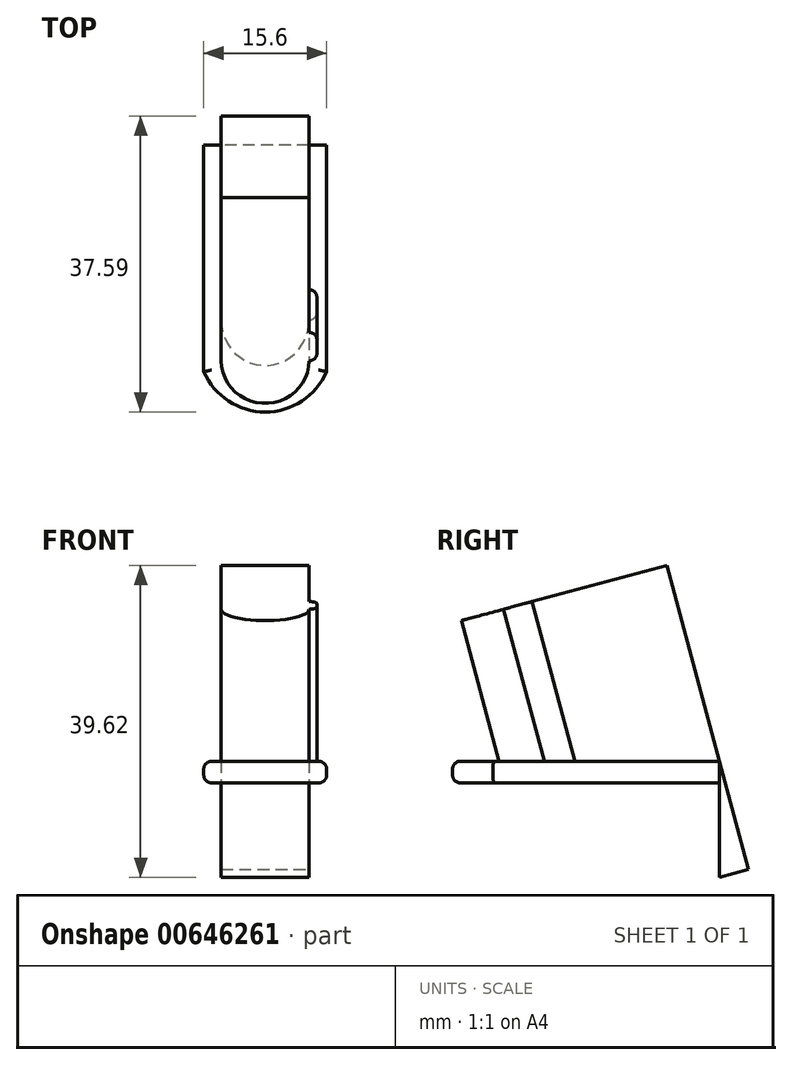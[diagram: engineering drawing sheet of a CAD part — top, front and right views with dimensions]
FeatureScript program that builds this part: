
annotation { "Feature Type Name" : "Feature", "Feature Type Description" : "" }
export const myFeature = defineFeature(function(context is Context, id is Id, definition is map)
    precondition{}
    {
        {
            var Q0;
            Q0=qCreatedBy(makeId("Top.planeOp"),FACE);
            var sketch = newSketch(context, id + "F0", { "sketchPlane" : qUnion([Q0])});
            skLineSegment(sketch, "E0.bottom", {"start": v(-7.8, 16.95) * mm, "end": v(7.8, 16.95) * mm});
            skLineSegment(sketch, "E0.top", {"start": v(-7.8, -16.95) * mm, "end": v(7.8, -16.95) * mm});
            skLineSegment(sketch, "E0.left", {"start": v(-7.8, 16.95) * mm, "end": v(-7.8, -16.95) * mm});
            skLineSegment(sketch, "E0.right", {"start": v(7.8, 16.95) * mm, "end": v(7.8, -16.95) * mm});
            skLineSegment(sketch, "E1.bottom", {"start": v(-5.58, 16.95) * mm, "end": v(5.58, 16.95) * mm});
            skLineSegment(sketch, "E1.top", {"start": v(-5.57, -5.28) * mm, "end": v(5.58, -5.28) * mm});
            skLineSegment(sketch, "E1.left", {"start": v(-5.58, 16.95) * mm, "end": v(-5.57, -5.28) * mm});
            skLineSegment(sketch, "E1.right", {"start": v(5.57, 16.95) * mm, "end": v(5.58, -5.28) * mm});
            skArc(sketch, "E2", {"start": v(-5.57, -5.28) * mm, "mid": v(0, -10.85) * mm, "end": v(5.58, -5.28) * mm});
            skArc(sketch, "E3", {"start": v(-7.8, -11.83) * mm, "mid": v(0, -16.95) * mm, "end": v(7.8, -11.83) * mm});
            skLineSegment(sketch, "E4.bottom", {"start": v(5.58, 16.95) * mm, "end": v(-5.58, 16.95) * mm});
            skLineSegment(sketch, "E4.top", {"start": v(5.58, 23) * mm, "end": v(-5.58, 23) * mm});
            skLineSegment(sketch, "E4.left", {"start": v(5.58, 16.95) * mm, "end": v(5.58, 23) * mm});
            skLineSegment(sketch, "E4.right", {"start": v(-5.58, 16.95) * mm, "end": v(-5.58, 23) * mm});
            skSolve(sketch);
        }
        {
            var Q0;
            Q0=sQuery(id+"F0.wireOp",EDGE,"E1.top");
            cPlane(context, id + "F1", {"entities" : qUnion([Q0]), "cplaneType" : CPlaneType.LINE_ANGLE, "offset" : 25 * mm, "angle" : 75 * degree, "oppositeDirection" : true, "width" : 150 * mm, "height" : 150 * mm});
        }
        {
            var Q0;
            Q0=qCreatedBy(id+"F1.planeOp",FACE);
            var sketch = newSketch(context, id + "F2", { "sketchPlane" : qUnion([Q0])});
            skLineSegment(sketch, "E5.bottom", {"start": v(-5.57, 5.1) * mm, "end": v(5.58, 5.1) * mm});
            skLineSegment(sketch, "E5.top", {"start": v(-5.57, -16.37) * mm, "end": v(5.57, -16.37) * mm});
            skLineSegment(sketch, "E5.left", {"start": v(-5.58, 5.1) * mm, "end": v(-5.57, -16.37) * mm});
            skLineSegment(sketch, "E5.right", {"start": v(5.58, 5.1) * mm, "end": v(5.58, -16.37) * mm});
            skArc(sketch, "E6", {"start": v(5.58, 5.1) * mm, "mid": v(0, 10.67) * mm, "end": v(-5.57, 5.1) * mm});
            skLineSegment(sketch, "E7.bottom", {"start": v(5.58, 5.1) * mm, "end": v(6.58, 5.1) * mm});
            skLineSegment(sketch, "E7.top", {"start": v(5.58, 1.35) * mm, "end": v(6.58, 1.35) * mm});
            skLineSegment(sketch, "E7.left", {"start": v(5.58, 5.1) * mm, "end": v(5.58, 1.35) * mm});
            skLineSegment(sketch, "E7.right", {"start": v(6.58, 5.1) * mm, "end": v(6.58, 1.35) * mm});
            skSolve(sketch);
        }
        {
            var Q0;
            Q0=makeQuery(id+"F2.imprint","IMPRINT",FACE,{"disambiguationData":[TD([[makeQuery(id+"F2.imprint","IMPRINT",EDGE,{"derivedFrom":sQuery(id+"F2.wireOp",EDGE,"E5.bottom")}),1.0]])]});
            var Q1;
            Q1=makeQuery(id+"F2.imprint","IMPRINT",FACE,{"disambiguationData":[TD([[makeQuery(id+"F2.imprint","IMPRINT",EDGE,{"derivedFrom":sQuery(id+"F2.wireOp",EDGE,"E5.bottom")}),-1.0]])]});
            var Q2;
            Q2=makeQuery(id+"F2.imprint","IMPRINT",FACE,{"disambiguationData":[TD([[makeQuery(id+"F2.imprint","IMPRINT",EDGE,{"derivedFrom":sQuery(id+"F2.wireOp",EDGE,"E7.bottom")}),-1.0]])]});
            extrude(context, id + "F3", {"entities" : qUnion([Q0, Q1, Q2]), "endBound" : BoundingType.SYMMETRIC, "depth" : 40 * mm, "offsetDistance" : 25 * mm});
        }
        {
            var Q0;
            Q0=makeQuery(id+"F0.imprint","IMPRINT",FACE,{"disambiguationData":[TD([[makeQuery(id+"F0.imprint","IMPRINT",EDGE,{"derivedFrom":sQuery(id+"F0.wireOp",EDGE,"E1.top")}),-1.0]])]});
            var Q1;
            {var subQ11=sQuery(id+"F0.wireOp",EDGE,"E1.left");Q1=makeQuery(id+"F0.imprint","IMPRINT",FACE,{"disambiguationData":[TD([[makeQuery(id+"F0.imprint","IMPRINT",EDGE,{"derivedFrom":subQ11}),-1.0]])]});}
            var Q2;
            Q2=makeQuery(id+"F0.imprint","IMPRINT",FACE,{"disambiguationData":[TD([[makeQuery(id+"F0.imprint","IMPRINT",EDGE,{"derivedFrom":sQuery(id+"F0.wireOp",EDGE,"E1.top")}),1.0]])]});
            var Q3;
            Q3=makeQuery(id+"F0.imprint","IMPRINT",FACE,{"disambiguationData":[TD([[makeQuery(id+"F0.imprint","IMPRINT",EDGE,{"derivedFrom":sQuery(id+"F0.wireOp",EDGE,"E4.bottom")}),-1.0]])]});
            extrude(context, id + "F4", {"entities" : qUnion([Q0, Q1, Q2, Q3]), "operationType" : NewBodyOperationType.REMOVE, "oppositeDirection" : true, "depth" : 25 * mm, "offsetDistance" : 25 * mm});
        }
        {
            var Q0;
            {var subQ11=sQuery(id+"F0.wireOp",EDGE,"E1.left");Q0=makeQuery(id+"F0.imprint","IMPRINT",FACE,{"disambiguationData":[TD([[makeQuery(id+"F0.imprint","IMPRINT",EDGE,{"derivedFrom":subQ11}),-1.0]])]});}
            var Q1;
            Q1=makeQuery(id+"F0.imprint","IMPRINT",FACE,{"disambiguationData":[TD([[makeQuery(id+"F0.imprint","IMPRINT",EDGE,{"derivedFrom":sQuery(id+"F0.wireOp",EDGE,"E1.top")}),-1.0]])]});
            var Q2;
            Q2=makeQuery(id+"F0.imprint","IMPRINT",FACE,{"disambiguationData":[TD([[makeQuery(id+"F0.imprint","IMPRINT",EDGE,{"derivedFrom":sQuery(id+"F0.wireOp",EDGE,"E1.top")}),1.0]])]});
            extrude(context, id + "F5", {"entities" : qUnion([Q0, Q1, Q2]), "operationType" : NewBodyOperationType.ADD, "oppositeDirection" : true, "depth" : 2.75 * mm, "offsetDistance" : 25 * mm});
        }
        {
            var Q0;
            Q0=makeQuery(id+"F5.opExtrude","CAP_EDGE",EDGE,{"disambiguationData":[OSD([sQuery(id+"F0.wireOp",EDGE,"E0.right")])],"isStart":true});
            var Q1;
            Q1=makeQuery(id+"F5.opExtrude","CAP_EDGE",EDGE,{"disambiguationData":[OSD([sQuery(id+"F0.wireOp",EDGE,"E3")])],"isStart":true});
            var Q2;
            Q2=makeQuery(id+"F5.opExtrude","CAP_EDGE",EDGE,{"disambiguationData":[OSD([sQuery(id+"F0.wireOp",EDGE,"E3")])],"isStart":false});
            var Q3;
            Q3=makeQuery(id+"F5.opExtrude","CAP_EDGE",EDGE,{"disambiguationData":[OSD([sQuery(id+"F0.wireOp",EDGE,"E0.right")])],"isStart":false});
            var Q4;
            Q4=makeQuery(id+"F5.opExtrude","CAP_EDGE",EDGE,{"disambiguationData":[OSD([sQuery(id+"F0.wireOp",EDGE,"E0.left")])],"isStart":true});
            var Q5;
            Q5=makeQuery(id+"F5.opExtrude","CAP_EDGE",EDGE,{"disambiguationData":[OSD([sQuery(id+"F0.wireOp",EDGE,"E0.left")])],"isStart":false});
            var Q6;
            Q6=makeQuery(id+"F3.opExtrude","SWEPT_EDGE",EDGE,{"disambiguationData":[OSD([sQuery(id+"F2.wireOp",EDGE,"E7.bottom"),sQuery(id+"F2.wireOp",EDGE,"E7.right")])]});
            var Q7;
            Q7=makeQuery(id+"F3.opExtrude","SWEPT_EDGE",EDGE,{"disambiguationData":[OSD([sQuery(id+"F2.wireOp",EDGE,"E7.top"),sQuery(id+"F2.wireOp",EDGE,"E7.right")])]});
            fillet(context, id + "F6", {"entities" : qUnion([Q0, Q1, Q2, Q3, Q4, Q5, Q6, Q7]), "radius" : 1 * mm, "tangentPropagation" : true, "allowEdgeOverflow" : false});
        }
    });
